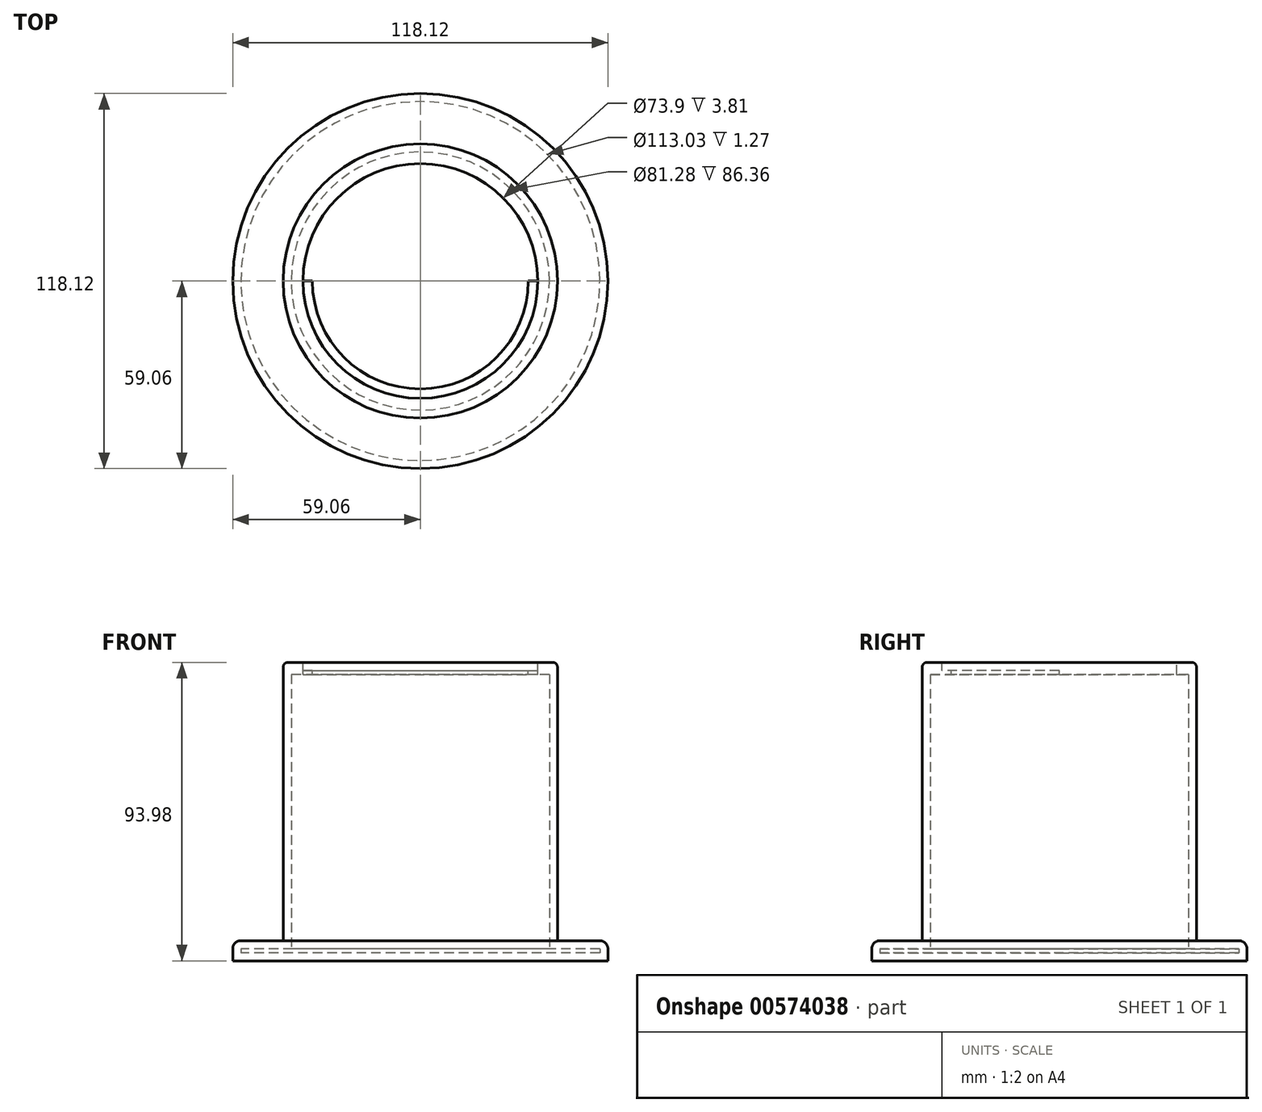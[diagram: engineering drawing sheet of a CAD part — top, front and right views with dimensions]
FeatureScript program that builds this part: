
annotation { "Feature Type Name" : "Feature", "Feature Type Description" : "" }
export const myFeature = defineFeature(function(context is Context, id is Id, definition is map)
    precondition{}
    {
        {
            var Q0;
            Q0=qCreatedBy(makeId("Top.planeOp"),FACE);
            var sketch = newSketch(context, id + "F0", { "sketchPlane" : qUnion([Q0])});
            skCircle(sketch, "E0", {"center": v(0, 0) * mm, "radius": 59.06 * mm});
            skCircle(sketch, "E1", {"center": v(0, 0) * mm, "radius": 43.18 * mm});
            skSolve(sketch);
        }
        {
            var Q0;
            Q0=makeQuery(id+"F0.imprint","IMPRINT",FACE,{"disambiguationData":[TD([[makeQuery(id+"F0.imprint","IMPRINT",EDGE,{"derivedFrom":sQuery(id+"F0.wireOp",EDGE,"E1")}),1.0]])]});
            extrude(context, id + "F1", {"entities" : qUnion([Q0]), "depth" : 90.17 * mm, "offsetDistance" : 25.4 * mm});
        }
        {
            var Q0;
            Q0=makeQuery(id+"F0.imprint","IMPRINT",FACE,{"disambiguationData":[TD([[makeQuery(id+"F0.imprint","IMPRINT",EDGE,{"derivedFrom":sQuery(id+"F0.wireOp",EDGE,"E0")}),1.0]])]});
            extrude(context, id + "F2", {"entities" : qUnion([Q0]), "operationType" : NewBodyOperationType.ADD, "depth" : 6.35 * mm, "offsetDistance" : 25.4 * mm});
        }
        {
            var Q0;
            Q0=makeQuery(id+"F1.opExtrude","CAP_FACE",FACE,{"disambiguationData":[OSD([sQuery(id+"F0.wireOp",EDGE,"E1")])],"isStart":false});
            shell(context, id + "F3", {"entities" : qUnion([Q0]), "thickness" : 2.54 * mm});
        }
        {
            var Q0;
            Q0=makeQuery(id+"F1.opExtrude","CAP_FACE",FACE,{"disambiguationData":[OSD([sQuery(id+"F0.wireOp",EDGE,"E1")])],"isStart":false});
            var sketch = newSketch(context, id + "F4", { "sketchPlane" : qUnion([Q0])});
            skCircle(sketch, "E2", {"center": v(0, 0) * mm, "radius": 43.18 * mm});
            skSolve(sketch);
        }
        {
            var Q0;
            Q0 = qSketchRegion(id + "F4", true);
            extrude(context, id + "F5", {"entities" : qUnion([Q0]), "operationType" : NewBodyOperationType.ADD, "depth" : 3.8 * mm, "offsetDistance" : 25.4 * mm});
        }
        {
            var Q0;
            Q0=makeQuery(id+"F5.opExtrude","CAP_FACE",FACE,{"disambiguationData":[OSD([sQuery(id+"F4.wireOp",EDGE,"E2")])],"isStart":false});
            var sketch = newSketch(context, id + "F6", { "sketchPlane" : qUnion([Q0])});
            skCircle(sketch, "E3", {"center": v(0, 0) * mm, "radius": 36.95 * mm});
            skCircle(sketch, "E4", {"center": v(0, 0) * mm, "radius": 33.99 * mm});
            skLineSegment(sketch, "E5", {"start": v(-33.99, 0) * mm, "end": v(-36.95, 0) * mm});
            skLineSegment(sketch, "E6", {"start": v(33.99, 0) * mm, "end": v(36.95, 0) * mm});
            skSolve(sketch);
        }
        {
            var Q0;
            {var subQ0=sQuery(id+"F6.wireOp",EDGE,"E4");var subQ1=makeQuery(id+"F6.imprint","INTERSECT",VERTEX,{"derivedFrom":[subQ0,sQuery(id+"F6.wireOp",EDGE,"E5")]});Q0=makeQuery(id+"F6.imprint","IMPRINT",FACE,{"disambiguationData":[TD([[makeQuery(id+"F6.imprint","IMPRINT",EDGE,{"disambiguationData":[TD([[subQ1,1.0]])],"derivedFrom":subQ0}),1.0]])]});}
            var Q1;
            {var subQ0=sQuery(id+"F6.wireOp",EDGE,"E5");Q1=makeQuery(id+"F6.imprint","IMPRINT",FACE,{"disambiguationData":[TD([[makeQuery(id+"F6.imprint","IMPRINT",EDGE,{"derivedFrom":subQ0}),-1.0]])]});}
            extrude(context, id + "F7", {"entities" : qUnion([Q0, Q1]), "operationType" : NewBodyOperationType.REMOVE, "endBound" : BoundingType.UP_TO_NEXT, "oppositeDirection" : true, "depth" : 25.4 * mm, "offsetDistance" : 25.4 * mm});
        }
        {
            var Q0;
            {var subQ0=sQuery(id+"F6.wireOp",EDGE,"E5");Q0=makeQuery(id+"F6.imprint","IMPRINT",FACE,{"disambiguationData":[TD([[makeQuery(id+"F6.imprint","IMPRINT",EDGE,{"derivedFrom":subQ0}),1.0]])]});}
            extrude(context, id + "F8", {"entities" : qUnion([Q0]), "operationType" : NewBodyOperationType.REMOVE, "oppositeDirection" : true, "depth" : 2.54 * mm, "offsetDistance" : 25.4 * mm});
        }
        {
            var Q0;
            Q0=makeQuery(id+"F2.opExtrude","CAP_EDGE",EDGE,{"disambiguationData":[OSD([sQuery(id+"F0.wireOp",EDGE,"E0")])],"isStart":false});
            fillet(context, id + "F9", {"entities" : qUnion([Q0]), "radius" : 2.54 * mm, "tangentPropagation" : true, "allowEdgeOverflow" : false});
        }
        {
            var Q0;
            Q0=makeQuery(id+"F5.opExtrude","CAP_EDGE",EDGE,{"disambiguationData":[OSD([sQuery(id+"F4.wireOp",EDGE,"E2")])],"isStart":false});
            fillet(context, id + "F10", {"entities" : qUnion([Q0]), "radius" : 1.52 * mm, "tangentPropagation" : true, "allowEdgeOverflow" : false});
        }
    });
